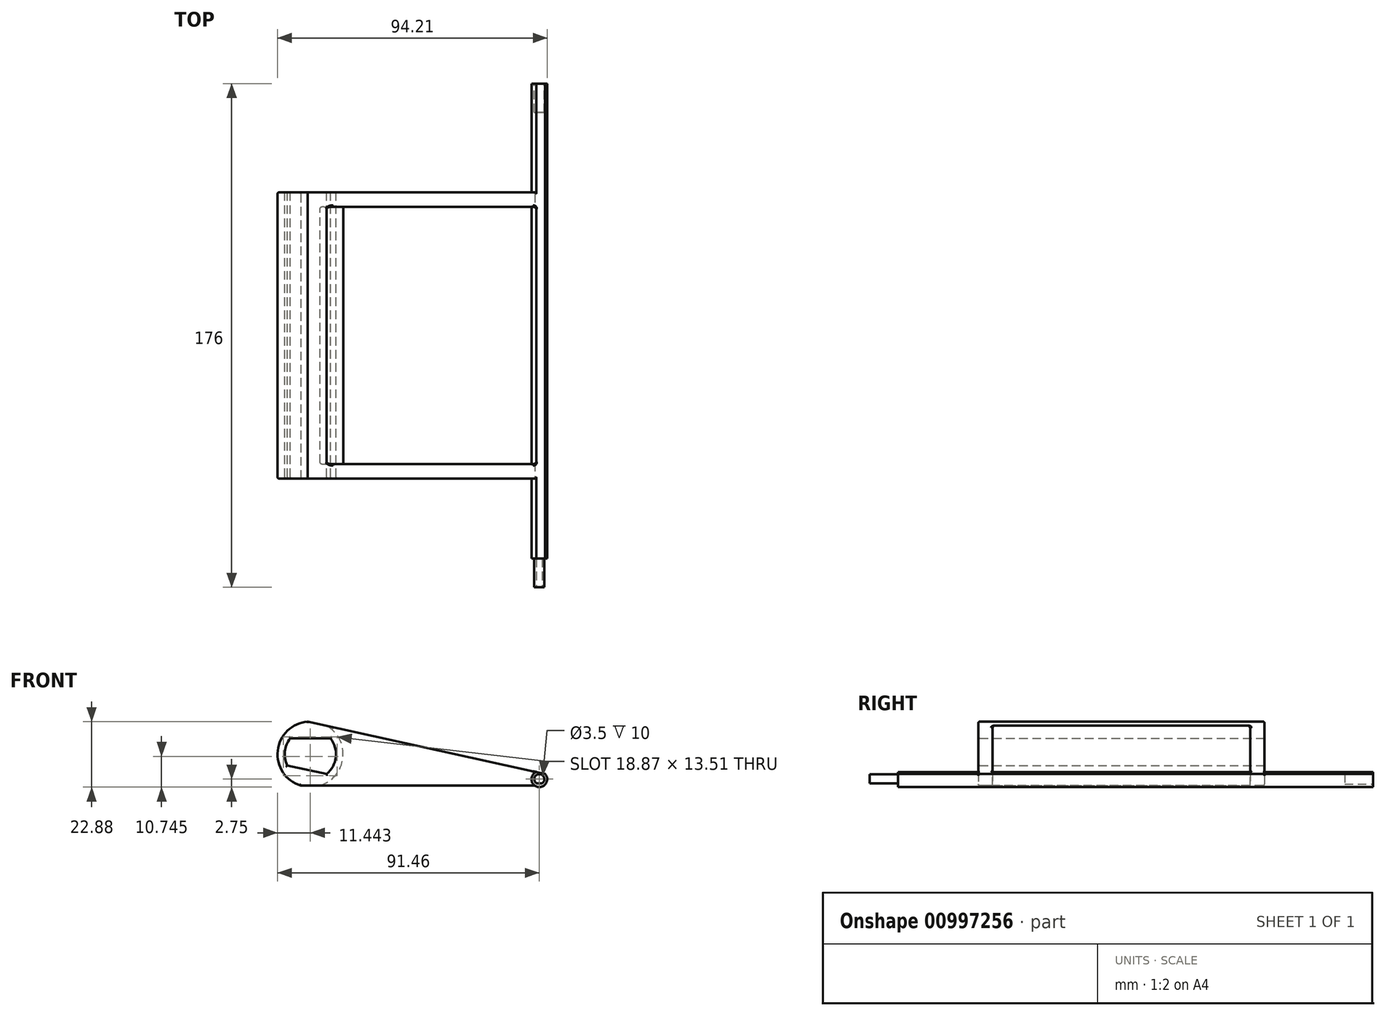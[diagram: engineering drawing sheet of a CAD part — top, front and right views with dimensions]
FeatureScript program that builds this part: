
annotation { "Feature Type Name" : "Feature", "Feature Type Description" : "" }
export const myFeature = defineFeature(function(context is Context, id is Id, definition is map)
    precondition{}
    {
        {
            var Q0;
            Q0=qCreatedBy(makeId("Front.planeOp"),FACE);
            var sketch = newSketch(context, id + "F0", { "sketchPlane" : qUnion([Q0])});
            skCircle(sketch, "E0", {"center": v(0, 0) * mm, "radius": 2.75 * mm});
            skCircle(sketch, "E1", {"center": v(-80, 8.7) * mm, "radius": 11.46 * mm});
            skLineSegment(sketch, "E2", {"start": v(-80, -2.75) * mm, "end": v(0, -2.75) * mm});
            skLineSegment(sketch, "E3", {"start": v(-77.54, 19.9) * mm, "end": v(0.6, 2.69) * mm});
            skCircle(sketch, "E4.0", {"center": v(-80, 8.7) * mm, "radius": 8.96 * mm});
            skLineSegment(sketch, "E5", {"start": v(-87.04, 14.25) * mm, "end": v(-72.96, 14.25) * mm});
            skLineSegment(sketch, "E6", {"start": v(-88.06, 4.8) * mm, "end": v(-74.32, 1.78) * mm});
            skSolve(sketch);
        }
        {
            var Q0;
            Q0=makeQuery(id+"F0.imprint","IMPRINT",FACE,{"disambiguationData":[TD([[makeQuery(id+"F0.imprint","IMPRINT",EDGE,{"derivedFrom":sQuery(id+"F0.wireOp",EDGE,"E0")}),1.0]])]});
            extrude(context, id + "F1", {"entities" : qUnion([Q0]), "endBound" : BoundingType.SYMMETRIC, "depth" : 176 * mm, "offsetDistance" : 25 * mm});
        }
        {
            var Q0;
            {var subQ0=sQuery(id+"F0.wireOp",EDGE,"E1");var subQ1=makeQuery(id+"F0.imprint","INTERSECT",VERTEX,{"derivedFrom":[subQ0,sQuery(id+"F0.wireOp",EDGE,"E2")]});Q0=makeQuery(id+"F0.imprint","IMPRINT",FACE,{"disambiguationData":[TD([[makeQuery(id+"F0.imprint","IMPRINT",EDGE,{"disambiguationData":[TD([[subQ1,1.0]])],"derivedFrom":subQ0}),1.0]])]});}
            var Q1;
            {var subQ0=sQuery(id+"F0.wireOp",EDGE,"E2");Q1=makeQuery(id+"F0.imprint","IMPRINT",FACE,{"disambiguationData":[TD([[makeQuery(id+"F0.imprint","IMPRINT",EDGE,{"derivedFrom":subQ0}),1.0]])]});}
            var Q2;
            {var subQ0=sQuery(id+"F0.wireOp",EDGE,"E5");Q2=makeQuery(id+"F0.imprint","IMPRINT",FACE,{"disambiguationData":[TD([[makeQuery(id+"F0.imprint","IMPRINT",EDGE,{"derivedFrom":subQ0}),1.0]])]});}
            var Q3;
            {var subQ0=sQuery(id+"F0.wireOp",EDGE,"E6");Q3=makeQuery(id+"F0.imprint","IMPRINT",FACE,{"disambiguationData":[TD([[makeQuery(id+"F0.imprint","IMPRINT",EDGE,{"derivedFrom":subQ0}),-1.0]])]});}
            extrude(context, id + "F2", {"entities" : qUnion([Q0, Q1, Q2, Q3]), "operationType" : NewBodyOperationType.ADD, "endBound" : BoundingType.SYMMETRIC, "depth" : 100 * mm, "offsetDistance" : 25 * mm});
        }
        {
            var Q0;
            {var subQ0=sQuery(id+"F0.wireOp",EDGE,"E2");Q0=makeQuery(id+"F0.imprint","IMPRINT",FACE,{"disambiguationData":[TD([[makeQuery(id+"F0.imprint","IMPRINT",EDGE,{"derivedFrom":subQ0}),1.0]])]});}
            extrude(context, id + "F3", {"entities" : qUnion([Q0]), "operationType" : NewBodyOperationType.REMOVE, "endBound" : BoundingType.SYMMETRIC, "oppositeDirection" : true, "depth" : 90 * mm, "offsetDistance" : 25 * mm});
        }
        {
            var Q0;
            Q0=makeQuery(id+"F1.opExtrude","CAP_FACE",FACE,{"disambiguationData":[OSD([sQuery(id+"F0.wireOp",EDGE,"E0")])],"isStart":false});
            var sketch = newSketch(context, id + "F4", { "sketchPlane" : qUnion([Q0])});
            skArc(sketch, "E7.0.0", {"start": v(-77.54, 19.9) * mm, "mid": v(-91.4, 9.95) * mm, "end": v(-80, -2.75) * mm});
            skLineSegment(sketch, "E7.0.1", {"start": v(-80, -2.75) * mm, "end": v(0, -2.75) * mm});
            skArc(sketch, "E7.0.2", {"start": v(0, -2.75) * mm, "mid": v(-2.73, 0.3) * mm, "end": v(0.6, 2.69) * mm});
            skLineSegment(sketch, "E7.0.3", {"start": v(0.6, 2.69) * mm, "end": v(-77.54, 19.9) * mm});
            skCircle(sketch, "E8.0", {"center": v(0, 0) * mm, "radius": 2.75 * mm});
            skLineSegment(sketch, "E9", {"start": v(-89.59, -2.25) * mm, "end": v(11.55, -2.25) * mm});
            skLineSegment(sketch, "E10", {"start": v(-84.98, 21.02) * mm, "end": v(10.41, 0) * mm});
            skSolve(sketch);
        }
        {
            var Q0;
            {var subQ0=sQuery(id+"F4.wireOp",EDGE,"E7.0.1");Q0=makeQuery(id+"F4.imprint","IMPRINT",FACE,{"disambiguationData":[TD([[makeQuery(id+"F4.imprint","IMPRINT",EDGE,{"derivedFrom":subQ0}),1.0]])]});}
            var Q1;
            {var subQ0=sQuery(id+"F4.wireOp",EDGE,"E8.0");var subQ1=makeQuery(id+"F4.imprint","INTERSECT",VERTEX,{"derivedFrom":[sQuery(id+"F4.wireOp",EDGE,"E7.0.1"),subQ0]});Q1=makeQuery(id+"F4.imprint","IMPRINT",FACE,{"disambiguationData":[TD([[makeQuery(id+"F4.imprint","IMPRINT",EDGE,{"disambiguationData":[TD([[subQ1,1.0]])],"derivedFrom":subQ0}),1.0]])]});}
            extrude(context, id + "F5", {"entities" : qUnion([Q0, Q1]), "operationType" : NewBodyOperationType.REMOVE, "endBound" : BoundingType.THROUGH_ALL, "oppositeDirection" : true, "depth" : 25 * mm, "offsetDistance" : 25 * mm});
        }
        {
            var Q0;
            {var subQ0=sQuery(id+"F4.wireOp",EDGE,"E7.0.3");Q0=makeQuery(id+"F4.imprint","IMPRINT",FACE,{"disambiguationData":[TD([[makeQuery(id+"F4.imprint","IMPRINT",EDGE,{"derivedFrom":subQ0}),1.0]])]});}
            var Q1;
            {var subQ0=sQuery(id+"F4.wireOp",EDGE,"E8.0");var subQ1=makeQuery(id+"F4.imprint","INTERSECT",VERTEX,{"derivedFrom":[sQuery(id+"F4.wireOp",EDGE,"E7.0.3"),subQ0]});Q1=makeQuery(id+"F4.imprint","IMPRINT",FACE,{"disambiguationData":[TD([[makeQuery(id+"F4.imprint","IMPRINT",EDGE,{"disambiguationData":[TD([[subQ1,1.0]])],"derivedFrom":subQ0}),1.0]])]});}
            extrude(context, id + "F6", {"entities" : qUnion([Q0, Q1]), "operationType" : NewBodyOperationType.REMOVE, "endBound" : BoundingType.THROUGH_ALL, "oppositeDirection" : true, "depth" : 25 * mm, "offsetDistance" : 25 * mm});
        }
        {
            var Q0;
            Q0=makeQuery(id+"F2.opExtrude","CAP_EDGE",EDGE,{"disambiguationData":[OSD([sQuery(id+"F0.wireOp",EDGE,"E1")])],"isStart":false});
            var Q1;
            Q1=makeQuery(id+"F2.opExtrude","CAP_EDGE",EDGE,{"disambiguationData":[OSD([sQuery(id+"F0.wireOp",EDGE,"E1")])],"isStart":true});
            var Q2;
            {var subQ0=sQuery(id+"F0.wireOp",EDGE,"E4.0");Q2=makeQuery(id+"F2.opExtrude","CAP_EDGE",EDGE,{"disambiguationData":[OSD([subQ0]),TDD([makeQuery(id+"F0.imprint","IMPRINT",EDGE,{"disambiguationData":[TD([[makeQuery(id+"F0.imprint","INTERSECT",VERTEX,{"disambiguationData":[OD(0.0)],"derivedFrom":[subQ0,sQuery(id+"F0.wireOp",EDGE,"E5")]}),-1.0]])],"derivedFrom":subQ0})])],"isStart":false});}
            var Q3;
            {var subQ0=sQuery(id+"F0.wireOp",EDGE,"E4.0");Q3=makeQuery(id+"F2.opExtrude","CAP_EDGE",EDGE,{"disambiguationData":[OSD([subQ0]),TDD([makeQuery(id+"F0.imprint","IMPRINT",EDGE,{"disambiguationData":[TD([[makeQuery(id+"F0.imprint","INTERSECT",VERTEX,{"disambiguationData":[OD(1.0)],"derivedFrom":[subQ0,sQuery(id+"F0.wireOp",EDGE,"E5")]}),1.0]])],"derivedFrom":subQ0})])],"isStart":false});}
            var Q4;
            Q4=makeQuery(id+"F2.opExtrude","CAP_EDGE",EDGE,{"disambiguationData":[OSD([sQuery(id+"F0.wireOp",EDGE,"E5")])],"isStart":false});
            var Q5;
            Q5=makeQuery(id+"F2.opExtrude","CAP_EDGE",EDGE,{"disambiguationData":[OSD([sQuery(id+"F0.wireOp",EDGE,"E6")])],"isStart":false});
            var Q6;
            Q6=makeQuery(id+"F2.opExtrude","CAP_EDGE",EDGE,{"disambiguationData":[OSD([sQuery(id+"F0.wireOp",EDGE,"E6")])],"isStart":true});
            var Q7;
            {var subQ0=sQuery(id+"F0.wireOp",EDGE,"E4.0");Q7=makeQuery(id+"F2.opExtrude","CAP_EDGE",EDGE,{"disambiguationData":[OSD([subQ0]),TDD([makeQuery(id+"F0.imprint","IMPRINT",EDGE,{"disambiguationData":[TD([[makeQuery(id+"F0.imprint","INTERSECT",VERTEX,{"disambiguationData":[OD(1.0)],"derivedFrom":[subQ0,sQuery(id+"F0.wireOp",EDGE,"E5")]}),1.0]])],"derivedFrom":subQ0})])],"isStart":true});}
            var Q8;
            {var subQ0=sQuery(id+"F0.wireOp",EDGE,"E4.0");Q8=makeQuery(id+"F2.opExtrude","CAP_EDGE",EDGE,{"disambiguationData":[OSD([subQ0]),TDD([makeQuery(id+"F0.imprint","IMPRINT",EDGE,{"disambiguationData":[TD([[makeQuery(id+"F0.imprint","INTERSECT",VERTEX,{"disambiguationData":[OD(0.0)],"derivedFrom":[subQ0,sQuery(id+"F0.wireOp",EDGE,"E5")]}),-1.0]])],"derivedFrom":subQ0})])],"isStart":true});}
            var Q9;
            Q9=makeQuery(id+"F2.opExtrude","CAP_EDGE",EDGE,{"disambiguationData":[OSD([sQuery(id+"F0.wireOp",EDGE,"E5")])],"isStart":true});
            var Q10;
            Q10=makeQuery(id+"F6.boolean.opBoolean","INTERSECT",EDGE,{"derivedFrom":[makeQuery(id+"F2.opExtrude","CAP_FACE",FACE,{"disambiguationData":[OSD([sQuery(id+"F0.wireOp",EDGE,"E0"),sQuery(id+"F0.wireOp",EDGE,"E1"),sQuery(id+"F0.wireOp",EDGE,"E2"),sQuery(id+"F0.wireOp",EDGE,"E3"),sQuery(id+"F0.wireOp",EDGE,"E4.0"),sQuery(id+"F0.wireOp",EDGE,"E5"),sQuery(id+"F0.wireOp",EDGE,"E6")])],"isStart":false}),makeQuery(id+"F6.opExtrude","SWEPT_FACE",FACE,{"disambiguationData":[OSD([sQuery(id+"F4.wireOp",EDGE,"E10")])]})]});
            var Q11;
            Q11=makeQuery(id+"F5.boolean.opBoolean","INTERSECT",EDGE,{"derivedFrom":[makeQuery(id+"F2.opExtrude","CAP_FACE",FACE,{"disambiguationData":[OSD([sQuery(id+"F0.wireOp",EDGE,"E0"),sQuery(id+"F0.wireOp",EDGE,"E1"),sQuery(id+"F0.wireOp",EDGE,"E2"),sQuery(id+"F0.wireOp",EDGE,"E3"),sQuery(id+"F0.wireOp",EDGE,"E4.0"),sQuery(id+"F0.wireOp",EDGE,"E5"),sQuery(id+"F0.wireOp",EDGE,"E6")])],"isStart":false}),makeQuery(id+"F5.opExtrude","SWEPT_FACE",FACE,{"disambiguationData":[OSD([sQuery(id+"F4.wireOp",EDGE,"E9")])]})]});
            var Q12;
            Q12=makeQuery(id+"F6.boolean.opBoolean","INTERSECT",EDGE,{"derivedFrom":[makeQuery(id+"F3.boolean.opBoolean","COPY",FACE,{"derivedFrom":makeQuery(id+"F3.opExtrude","CAP_FACE",FACE,{"disambiguationData":[OSD([sQuery(id+"F0.wireOp",EDGE,"E0"),sQuery(id+"F0.wireOp",EDGE,"E1"),sQuery(id+"F0.wireOp",EDGE,"E2"),sQuery(id+"F0.wireOp",EDGE,"E3")])],"isStart":true})}),makeQuery(id+"F6.opExtrude","SWEPT_FACE",FACE,{"disambiguationData":[OSD([sQuery(id+"F4.wireOp",EDGE,"E10")])]})]});
            var Q13;
            Q13=makeQuery(id+"F6.boolean.opBoolean","INTERSECT",EDGE,{"derivedFrom":[makeQuery(id+"F2.opExtrude","CAP_FACE",FACE,{"disambiguationData":[OSD([sQuery(id+"F0.wireOp",EDGE,"E0"),sQuery(id+"F0.wireOp",EDGE,"E1"),sQuery(id+"F0.wireOp",EDGE,"E2"),sQuery(id+"F0.wireOp",EDGE,"E3"),sQuery(id+"F0.wireOp",EDGE,"E4.0"),sQuery(id+"F0.wireOp",EDGE,"E5"),sQuery(id+"F0.wireOp",EDGE,"E6")])],"isStart":true}),makeQuery(id+"F6.opExtrude","SWEPT_FACE",FACE,{"disambiguationData":[OSD([sQuery(id+"F4.wireOp",EDGE,"E10")])]})]});
            var Q14;
            Q14=makeQuery(id+"F5.boolean.opBoolean","INTERSECT",EDGE,{"derivedFrom":[makeQuery(id+"F2.opExtrude","CAP_FACE",FACE,{"disambiguationData":[OSD([sQuery(id+"F0.wireOp",EDGE,"E0"),sQuery(id+"F0.wireOp",EDGE,"E1"),sQuery(id+"F0.wireOp",EDGE,"E2"),sQuery(id+"F0.wireOp",EDGE,"E3"),sQuery(id+"F0.wireOp",EDGE,"E4.0"),sQuery(id+"F0.wireOp",EDGE,"E5"),sQuery(id+"F0.wireOp",EDGE,"E6")])],"isStart":true}),makeQuery(id+"F5.opExtrude","SWEPT_FACE",FACE,{"disambiguationData":[OSD([sQuery(id+"F4.wireOp",EDGE,"E9")])]})]});
            var Q15;
            Q15=makeQuery(id+"F6.boolean.opBoolean","INTERSECT",EDGE,{"derivedFrom":[makeQuery(id+"F3.boolean.opBoolean","COPY",FACE,{"derivedFrom":makeQuery(id+"F3.opExtrude","CAP_FACE",FACE,{"disambiguationData":[OSD([sQuery(id+"F0.wireOp",EDGE,"E0"),sQuery(id+"F0.wireOp",EDGE,"E1"),sQuery(id+"F0.wireOp",EDGE,"E2"),sQuery(id+"F0.wireOp",EDGE,"E3")])],"isStart":false})}),makeQuery(id+"F6.opExtrude","SWEPT_FACE",FACE,{"disambiguationData":[OSD([sQuery(id+"F4.wireOp",EDGE,"E10")])]})]});
            var Q16;
            Q16=makeQuery(id+"F3.boolean.opBoolean","COPY",EDGE,{"derivedFrom":makeQuery(id+"F3.opExtrude","CAP_EDGE",EDGE,{"disambiguationData":[OSD([sQuery(id+"F0.wireOp",EDGE,"E1")])],"isStart":false})});
            var Q17;
            Q17=makeQuery(id+"F3.boolean.opBoolean","COPY",EDGE,{"derivedFrom":makeQuery(id+"F3.opExtrude","CAP_EDGE",EDGE,{"disambiguationData":[OSD([sQuery(id+"F0.wireOp",EDGE,"E1")])],"isStart":true})});
            var Q18;
            Q18=makeQuery(id+"F3.boolean.opBoolean","COPY",EDGE,{"derivedFrom":makeQuery(id+"F3.opExtrude","CAP_EDGE",EDGE,{"disambiguationData":[OSD([sQuery(id+"F0.wireOp",EDGE,"E0")])],"isStart":false})});
            var Q19;
            Q19=makeQuery(id+"F3.boolean.opBoolean","COPY",EDGE,{"derivedFrom":makeQuery(id+"F3.opExtrude","CAP_EDGE",EDGE,{"disambiguationData":[OSD([sQuery(id+"F0.wireOp",EDGE,"E0")])],"isStart":true})});
            var Q20;
            Q20=makeQuery(id+"F2.opExtrude","CAP_EDGE",EDGE,{"disambiguationData":[OSD([sQuery(id+"F0.wireOp",EDGE,"E0")])],"isStart":true});
            var Q21;
            Q21=makeQuery(id+"F2.opExtrude","CAP_EDGE",EDGE,{"disambiguationData":[OSD([sQuery(id+"F0.wireOp",EDGE,"E0")])],"isStart":false});
            fillet(context, id + "F7", {"entities" : qUnion([Q0, Q1, Q2, Q3, Q4, Q5, Q6, Q7, Q8, Q9, Q10, Q11, Q12, Q13, Q14, Q15, Q16, Q17, Q18, Q19, Q20, Q21]), "radius" : 0.5 * mm, "tangentPropagation" : true, "allowEdgeOverflow" : false});
        }
        {
            var Q0;
            Q0=makeQuery(id+"F1.opExtrude","CAP_FACE",FACE,{"disambiguationData":[OSD([sQuery(id+"F0.wireOp",EDGE,"E0")])],"isStart":false});
            var sketch = newSketch(context, id + "F8", { "sketchPlane" : qUnion([Q0])});
            skCircle(sketch, "E11", {"center": v(0, 0) * mm, "radius": 1.75 * mm});
            skLineSegment(sketch, "E12", {"start": v(-0.98, -1.45) * mm, "end": v(0.98, -1.45) * mm});
            skSolve(sketch);
        }
        {
            var Q0;
            Q0=makeQuery(id+"F8.imprint","IMPRINT",FACE,{"disambiguationData":[TD([[makeQuery(id+"F8.imprint","IMPRINT",EDGE,{"derivedFrom":sQuery(id+"F8.wireOp",EDGE,"E11")}),-1.0]])]});
            var Q1;
            {var subQ0=sQuery(id+"F8.wireOp",EDGE,"E12");Q1=makeQuery(id+"F8.imprint","IMPRINT",FACE,{"disambiguationData":[TD([[makeQuery(id+"F8.imprint","IMPRINT",EDGE,{"derivedFrom":subQ0}),-1.0]])]});}
            extrude(context, id + "F9", {"entities" : qUnion([Q0, Q1]), "operationType" : NewBodyOperationType.REMOVE, "oppositeDirection" : true, "depth" : 10 * mm, "offsetDistance" : 25 * mm});
        }
        {
            var Q0;
            Q0=makeQuery(id+"F1.opExtrude","CAP_FACE",FACE,{"disambiguationData":[OSD([sQuery(id+"F0.wireOp",EDGE,"E0")])],"isStart":true});
            var sketch = newSketch(context, id + "F10", { "sketchPlane" : qUnion([Q0])});
            skCircle(sketch, "E13.0", {"center": v(0, 0) * mm, "radius": 1.75 * mm});
            skLineSegment(sketch, "E14.0", {"start": v(0.98, -1.45) * mm, "end": v(-0.98, -1.45) * mm});
            skSolve(sketch);
        }
        {
            var Q0;
            Q0=makeQuery(id+"F10.imprint","IMPRINT",FACE,{"disambiguationData":[TD([[makeQuery(id+"F10.imprint","IMPRINT",EDGE,{"derivedFrom":sQuery(id+"F10.wireOp",EDGE,"E13.0")}),1.0]])]});
            var Q1;
            {var subQ0=sQuery(id+"F10.wireOp",EDGE,"E14.0");Q1=makeQuery(id+"F10.imprint","IMPRINT",FACE,{"disambiguationData":[TD([[makeQuery(id+"F10.imprint","IMPRINT",EDGE,{"derivedFrom":subQ0}),1.0]])]});}
            extrude(context, id + "F11", {"entities" : qUnion([Q0, Q1]), "operationType" : NewBodyOperationType.REMOVE, "oppositeDirection" : true, "depth" : 10 * mm, "offsetDistance" : 25 * mm});
        }
    });
